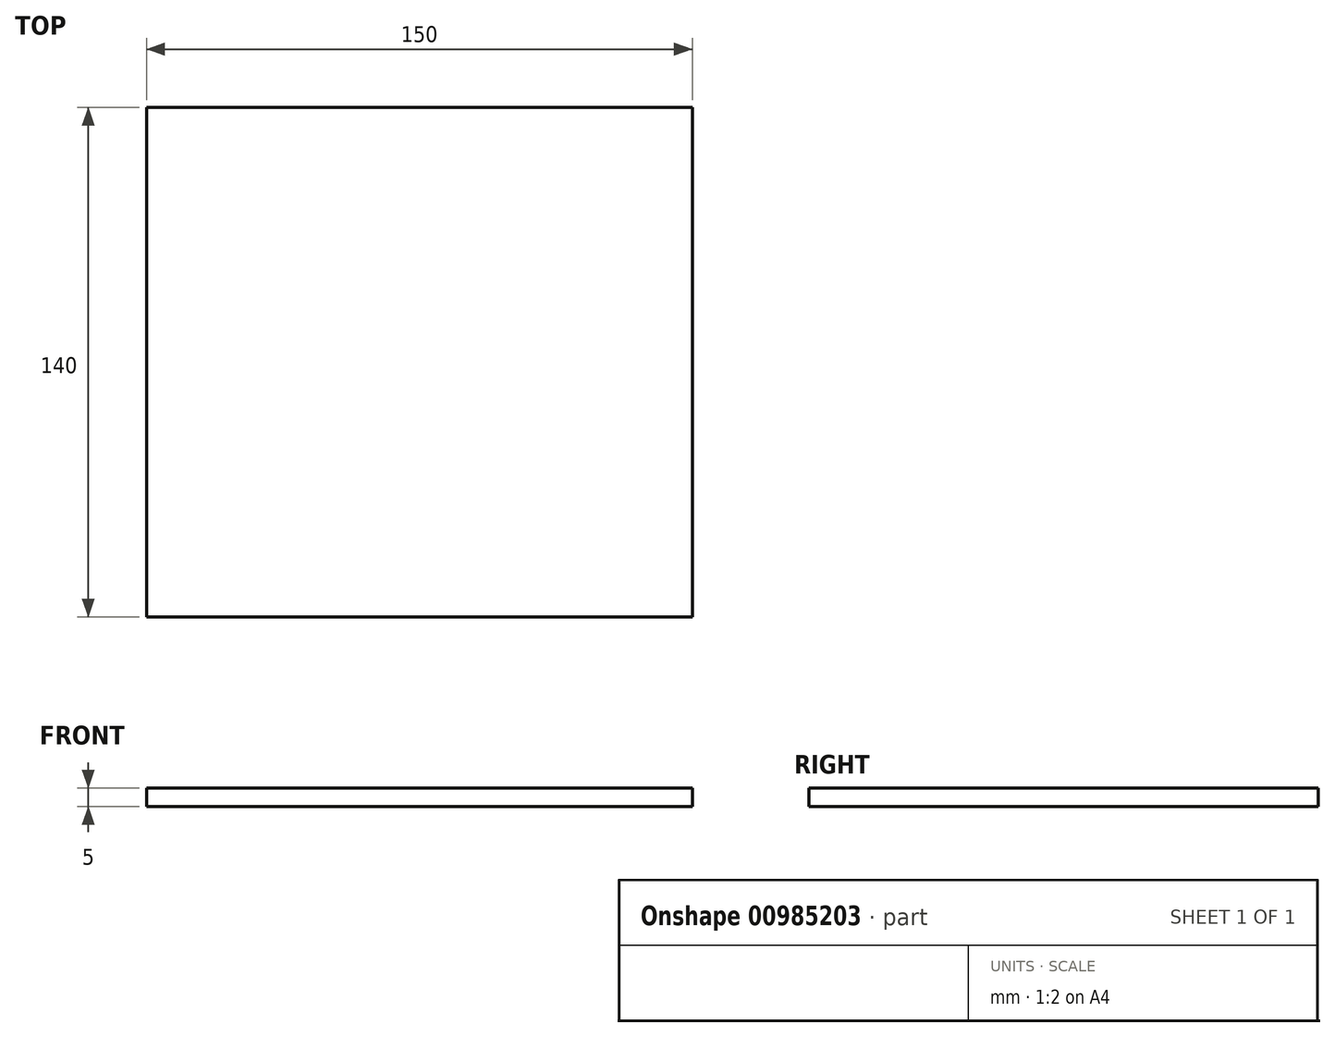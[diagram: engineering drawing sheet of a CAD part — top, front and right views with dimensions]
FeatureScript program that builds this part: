
annotation { "Feature Type Name" : "Feature", "Feature Type Description" : "" }
export const myFeature = defineFeature(function(context is Context, id is Id, definition is map)
    precondition{}
    {
        {
            var Q0;
            Q0=qCreatedBy(makeId("Top.planeOp"),FACE);
            var sketch = newSketch(context, id + "F0", { "sketchPlane" : qUnion([Q0])});
            skLineSegment(sketch, "E0.bottom", {"start": v(-75, 0) * mm, "end": v(75, 0) * mm});
            skLineSegment(sketch, "E0.top", {"start": v(-75, 140) * mm, "end": v(75, 140) * mm});
            skLineSegment(sketch, "E0.left", {"start": v(-75, 0) * mm, "end": v(-75, 140) * mm});
            skLineSegment(sketch, "E0.right", {"start": v(75, 0) * mm, "end": v(75, 140) * mm});
            skSolve(sketch);
        }
        {
            var Q0;
            Q0 = qSketchRegion(id + "F0", true);
            extrude(context, id + "F1", {"entities" : qUnion([Q0]), "depth" : 5 * mm, "offsetDistance" : 25 * mm});
        }
    });
